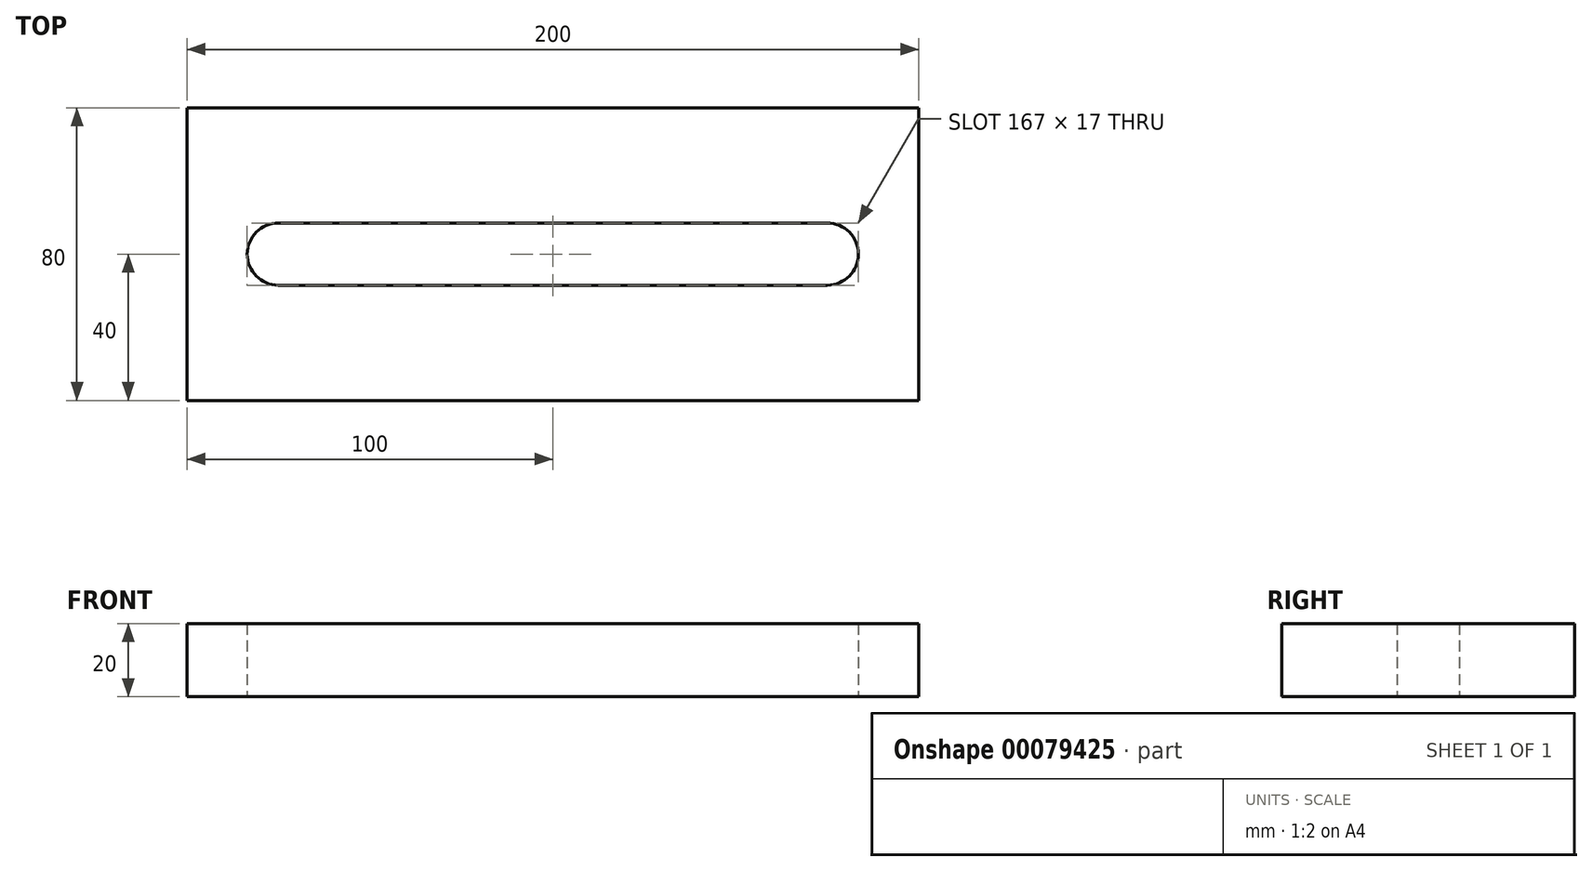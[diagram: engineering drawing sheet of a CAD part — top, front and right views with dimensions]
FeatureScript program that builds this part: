
annotation { "Feature Type Name" : "Feature", "Feature Type Description" : "" }
export const myFeature = defineFeature(function(context is Context, id is Id, definition is map)
    precondition{}
    {
        {
            var Q0;
            Q0=qCreatedBy(makeId("Top.planeOp"),FACE);
            var sketch = newSketch(context, id + "F0", { "sketchPlane" : qUnion([Q0])});
            skLineSegment(sketch, "E0.bottom", {"start": v(100, 40) * mm, "end": v(-100, 40) * mm});
            skLineSegment(sketch, "E0.top", {"start": v(100, -40) * mm, "end": v(-100, -40) * mm});
            skLineSegment(sketch, "E0.left", {"start": v(100, 40) * mm, "end": v(100, -40) * mm});
            skLineSegment(sketch, "E0.right", {"start": v(-100, 40) * mm, "end": v(-100, -40) * mm});
            skPoint(sketch, "E0.middle", {"position": v(0, 0) * mm});
            skCircle(sketch, "E1", {"center": v(-75, 0) * mm, "radius": 8.5 * mm});
            skCircle(sketch, "E2", {"center": v(75, 0) * mm, "radius": 8.5 * mm});
            skLineSegment(sketch, "E3", {"start": v(-75, 8.5) * mm, "end": v(75, 8.5) * mm});
            skLineSegment(sketch, "E4", {"start": v(-75, -8.5) * mm, "end": v(75, -8.5) * mm});
            skSolve(sketch);
        }
        {
            var Q0;
            Q0=makeQuery(id+"F0.imprint","IMPRINT",FACE,{"disambiguationData":[TD([[makeQuery(id+"F0.imprint","IMPRINT",EDGE,{"derivedFrom":sQuery(id+"F0.wireOp",EDGE,"E0.bottom")}),1.0]])]});
            extrude(context, id + "F1", {"entities" : qUnion([Q0]), "depth" : 20 * mm});
        }
    });
